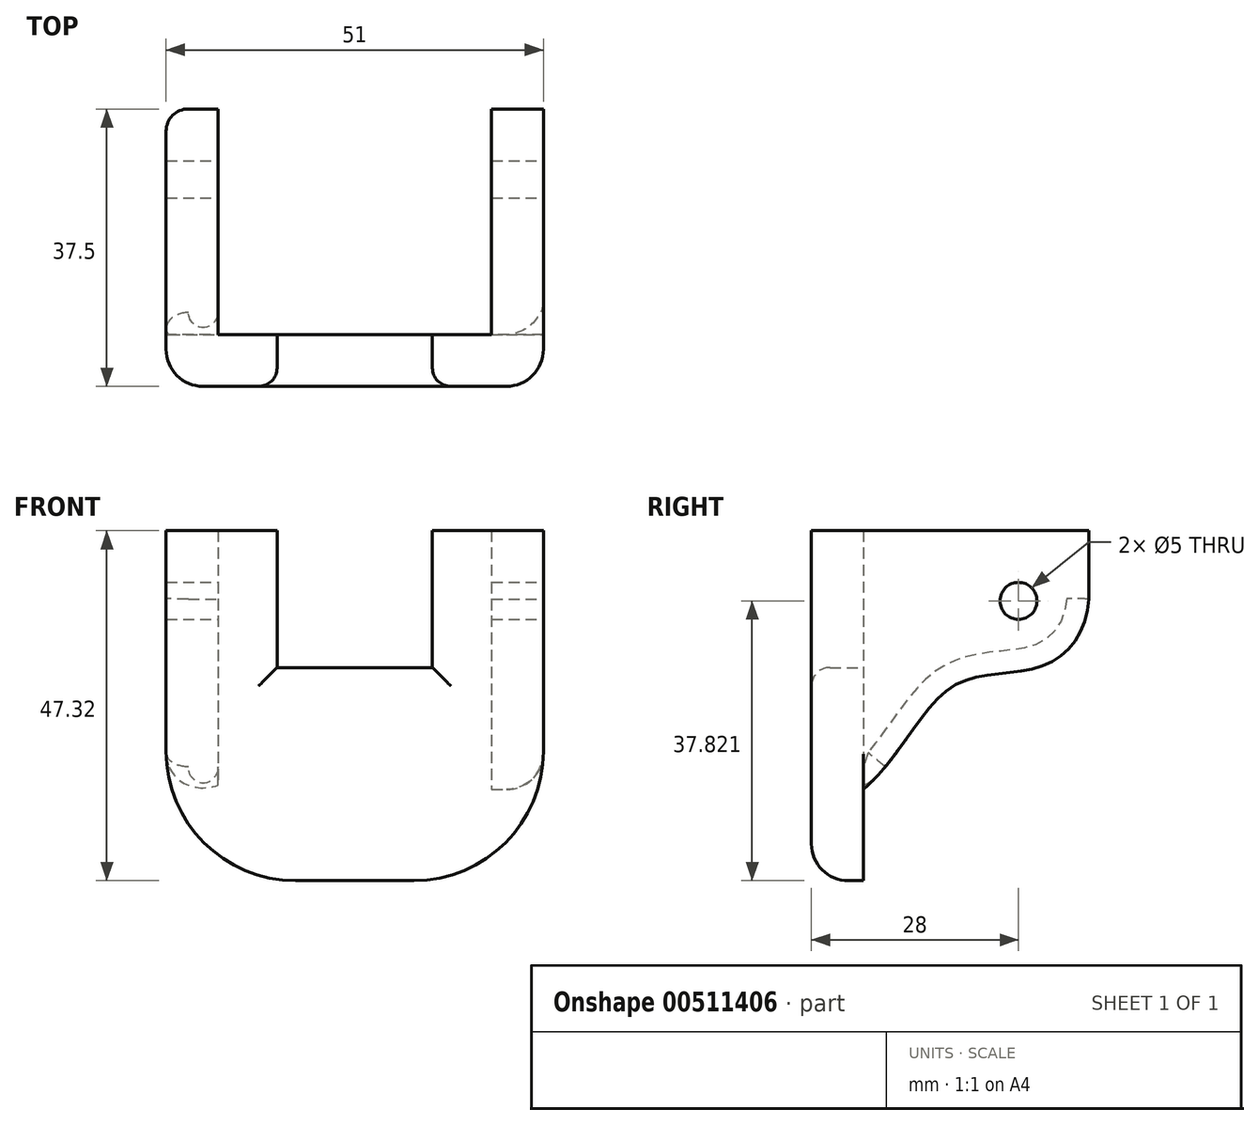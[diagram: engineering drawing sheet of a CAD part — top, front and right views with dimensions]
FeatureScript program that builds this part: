
annotation { "Feature Type Name" : "Feature", "Feature Type Description" : "" }
export const myFeature = defineFeature(function(context is Context, id is Id, definition is map)
    precondition{}
    {
        {
            var Q0;
            Q0=qCreatedBy(makeId("Front.planeOp"),FACE);
            var sketch = newSketch(context, id + "F0", { "sketchPlane" : qUnion([Q0])});
            skLineSegment(sketch, "E0.bottom", {"start": v(8, -23.66) * mm, "end": v(-8, -23.66) * mm});
            skLineSegment(sketch, "E0.top", {"start": v(25.5, 23.66) * mm, "end": v(10.5, 23.66) * mm});
            skLineSegment(sketch, "E0.left", {"start": v(25.5, -6.16) * mm, "end": v(25.5, 23.66) * mm});
            skLineSegment(sketch, "E0.right", {"start": v(-25.5, -6.16) * mm, "end": v(-25.5, 23.66) * mm});
            skPoint(sketch, "E0.middle", {"position": v(0, 0) * mm});
            skLineSegment(sketch, "E1.top", {"start": v(-10.5, 5.16) * mm, "end": v(10.5, 5.16) * mm});
            skLineSegment(sketch, "E1.left", {"start": v(-10.5, 23.66) * mm, "end": v(-10.5, 5.16) * mm});
            skLineSegment(sketch, "E1.right", {"start": v(10.5, 23.66) * mm, "end": v(10.5, 5.16) * mm});
            skPoint(sketch, "E2", {"position": v(0, 23.66) * mm});
            skPoint(sketch, "E3.visualSharp", {"position": v(-25.5, -23.66) * mm});
            skArc(sketch, "E3.filletArc", {"start": v(-25.5, -6.16) * mm, "mid": v(-20.37, -18.54) * mm, "end": v(-8, -23.66) * mm});
            skPoint(sketch, "E4.visualSharp", {"position": v(25.5, -23.66) * mm});
            skArc(sketch, "E4.filletArc", {"start": v(8, -23.66) * mm, "mid": v(20.37, -18.54) * mm, "end": v(25.5, -6.16) * mm});
            skPoint(sketch, "E5", {"position": v(25.5, 14.16) * mm});
            skPoint(sketch, "E6", {"position": v(-25.5, 14.16) * mm});
            skLineSegment(sketch, "E7.trimOffspring", {"start": v(-10.5, 23.66) * mm, "end": v(-25.5, 23.66) * mm});
            skSolve(sketch);
        }
        {
            var Q0;
            Q0=makeQuery(id+"F0.imprint","IMPRINT",FACE,{"disambiguationData":[TD([[makeQuery(id+"F0.imprint","IMPRINT",EDGE,{"derivedFrom":sQuery(id+"F0.wireOp",EDGE,"E0.bottom")}),-1.0]])]});
            extrude(context, id + "F1", {"entities" : qUnion([Q0]), "depth" : 7 * mm});
        }
        {
            var Q0;
            Q0=makeQuery(id+"F1.opExtrude","CAP_FACE",FACE,{"disambiguationData":[OSD([sQuery(id+"F0.wireOp",EDGE,"E0.bottom"),sQuery(id+"F0.wireOp",EDGE,"E0.top"),sQuery(id+"F0.wireOp",EDGE,"E0.left"),sQuery(id+"F0.wireOp",EDGE,"E0.right"),sQuery(id+"F0.wireOp",EDGE,"E1.top"),sQuery(id+"F0.wireOp",EDGE,"E1.left"),sQuery(id+"F0.wireOp",EDGE,"E1.right"),sQuery(id+"F0.wireOp",EDGE,"E3.filletArc"),sQuery(id+"F0.wireOp",EDGE,"E4.filletArc"),sQuery(id+"F0.wireOp",EDGE,"E7.trimOffspring")])],"isStart":false});
            cPlane(context, id + "F2", {"entities" : qUnion([Q0]), "cplaneType" : CPlaneType.OFFSET, "offset" : 0 * mm, "width" : 150 * mm, "height" : 150 * mm});
        }
        {
            var Q0;
            Q0=qCreatedBy(id+"F2.planeOp",FACE);
            var sketch = newSketch(context, id + "F3", { "sketchPlane" : qUnion([Q0])});
            skLineSegment(sketch, "E8.bottom", {"start": v(-10.5, 23.66) * mm, "end": v(-17.5, 23.66) * mm});
            skLineSegment(sketch, "E8.top", {"start": v(-18.5, -11.34) * mm, "end": v(-20.5, -11.34) * mm});
            skLineSegment(sketch, "E8.left", {"start": v(-18.5, 23.66) * mm, "end": v(-18.5, -11.34) * mm});
            skLineSegment(sketch, "E8.right", {"start": v(-25.5, 23.66) * mm, "end": v(-25.5, -6.34) * mm});
            skLineSegment(sketch, "E9.bottom", {"start": v(18.5, 23.66) * mm, "end": v(21.36, 23.66) * mm});
            skLineSegment(sketch, "E9.top", {"start": v(18.5, -11.34) * mm, "end": v(20.5, -11.34) * mm});
            skLineSegment(sketch, "E9.left", {"start": v(18.5, 23.66) * mm, "end": v(18.5, -11.34) * mm});
            skLineSegment(sketch, "E9.right", {"start": v(25.5, 23.66) * mm, "end": v(25.5, -6.34) * mm});
            skPoint(sketch, "E10", {"position": v(-17.5, 23.66) * mm});
            skPoint(sketch, "E11", {"position": v(21.36, 23.66) * mm});
            skLineSegment(sketch, "E12", {"start": v(-25.5, 23.66) * mm, "end": v(-17.5, 23.66) * mm});
            skLineSegment(sketch, "E13", {"start": v(25.5, 23.66) * mm, "end": v(18.5, 23.66) * mm});
            skPoint(sketch, "E14.visualSharp", {"position": v(25.5, -11.34) * mm});
            skArc(sketch, "E14.filletArc", {"start": v(20.5, -11.34) * mm, "mid": v(24.04, -9.87) * mm, "end": v(25.5, -6.34) * mm});
            skPoint(sketch, "E15.visualSharp", {"position": v(-25.5, -11.34) * mm});
            skArc(sketch, "E15.filletArc", {"start": v(-25.5, -6.34) * mm, "mid": v(-24.04, -9.87) * mm, "end": v(-20.5, -11.34) * mm});
            skSolve(sketch);
        }
        {
            var Q0;
            Q0 = qSketchRegion(id + "F3", true);
            extrude(context, id + "F4", {"entities" : qUnion([Q0]), "operationType" : NewBodyOperationType.ADD, "oppositeDirection" : true, "depth" : 37.5 * mm});
        }
        {
            var Q0;
            Q0=makeQuery(id+"F4.opExtrude","SWEPT_FACE",FACE,{"disambiguationData":[OSD([sQuery(id+"F3.wireOp",EDGE,"E9.right")])]});
            var sketch = newSketch(context, id + "F5", { "sketchPlane" : qUnion([Q0])});
            skLineSegment(sketch, "E16", {"start": v(0, 23.66) * mm, "end": v(0, 14.16) * mm, "construction": true});
            skLineSegment(sketch, "E17", {"start": v(0, 14.16) * mm, "end": v(21, 14.16) * mm, "construction": true});
            skCircle(sketch, "E18", {"center": v(21, 14.16) * mm, "radius": 2.5 * mm});
            skSolve(sketch);
        }
        {
            var Q0;
            Q0 = qSketchRegion(id + "F5", true);
            extrude(context, id + "F6", {"entities" : qUnion([Q0]), "operationType" : NewBodyOperationType.REMOVE, "oppositeDirection" : true, "depth" : 60 * mm});
        }
        {
            var Q0;
            Q0=makeQuery(id+"F4.opExtrude","SWEPT_FACE",FACE,{"disambiguationData":[OSD([sQuery(id+"F3.wireOp",EDGE,"E9.right")])]});
            var sketch = newSketch(context, id + "F7", { "sketchPlane" : qUnion([Q0])});
            skFitSpline(sketch, "E19", {"points": [v(30.5, 14.42) * mm, v(24.6, 5.5) * mm, v(12.38, 2.77) * mm, v(0, -11.34) * mm, v(-33.32, -23.94) * mm], "startDerivative": vector(-2.64, -64.95) * mm, "endDerivative": vector(-112.83, -34.47) * mm});
            skLineSegment(sketch, "E20", {"start": v(0, -11.34) * mm, "end": v(30.5, -11.34) * mm});
            skLineSegment(sketch, "E21", {"start": v(30.5, -11.34) * mm, "end": v(30.5, 14.42) * mm});
            skSolve(sketch);
        }
        {
            var Q0;
            Q0 = qSketchRegion(id + "F7", true);
            extrude(context, id + "F8", {"entities" : qUnion([Q0]), "operationType" : NewBodyOperationType.REMOVE, "oppositeDirection" : true, "depth" : 60 * mm});
        }
        {
            var Q0;
            Q0=makeQuery(id+"F1.opExtrude","CAP_EDGE",EDGE,{"disambiguationData":[OSD([sQuery(id+"F0.wireOp",EDGE,"E4.filletArc")])],"isStart":false});
            fillet(context, id + "F9", {"entities" : qUnion([Q0]), "radius" : 5 * mm, "tangentPropagation" : true, "allowEdgeOverflow" : false});
        }
        {
            var Q0;
            Q0=makeQuery(id+"F1.opExtrude","CAP_EDGE",EDGE,{"disambiguationData":[OSD([sQuery(id+"F0.wireOp",EDGE,"E1.top")])],"isStart":false});
            var Q1;
            Q1=makeQuery(id+"F1.opExtrude","CAP_EDGE",EDGE,{"disambiguationData":[OSD([sQuery(id+"F0.wireOp",EDGE,"E1.left")])],"isStart":false});
            var Q2;
            Q2=makeQuery(id+"F1.opExtrude","CAP_EDGE",EDGE,{"disambiguationData":[OSD([sQuery(id+"F0.wireOp",EDGE,"E1.right")])],"isStart":false});
            fillet(context, id + "F10", {"entities" : qUnion([Q0, Q1, Q2]), "radius" : 2.5 * mm, "tangentPropagation" : true, "allowEdgeOverflow" : false});
        }
        {
            var Q0;
            Q0=makeQuery(id+"F8.boolean.opBoolean","INTERSECT",EDGE,{"derivedFrom":[makeQuery(id+"F4.boolean.opBoolean","MERGE",FACE,{"derivedFrom":[makeQuery(id+"F1.opExtrude","SWEPT_FACE",FACE,{"disambiguationData":[OSD([sQuery(id+"F0.wireOp",EDGE,"E0.right")])]}),makeQuery(id+"F4.opExtrude","SWEPT_FACE",FACE,{"disambiguationData":[OSD([sQuery(id+"F3.wireOp",EDGE,"E8.right")])]})]}),makeQuery(id+"F8.opExtrude","SWEPT_FACE",FACE,{"disambiguationData":[OSD([sQuery(id+"F7.wireOp",EDGE,"E19")])]})]});
            var Q1;
            Q1=makeQuery(id+"F4.opExtrude","CAP_EDGE",EDGE,{"disambiguationData":[OSD([sQuery(id+"F3.wireOp",EDGE,"E8.right")])],"isStart":false});
            var Q2;
            Q2=makeQuery(id+"F8.boolean.opBoolean","COPY",EDGE,{"derivedFrom":makeQuery(id+"F8.opExtrude","CAP_EDGE",EDGE,{"disambiguationData":[OSD([sQuery(id+"F7.wireOp",EDGE,"E19")])],"isStart":true})});
            fillet(context, id + "F11", {"entities" : qUnion([Q0, Q1, Q2]), "radius" : 3 * mm, "tangentPropagation" : true, "allowEdgeOverflow" : false});
        }
    });
